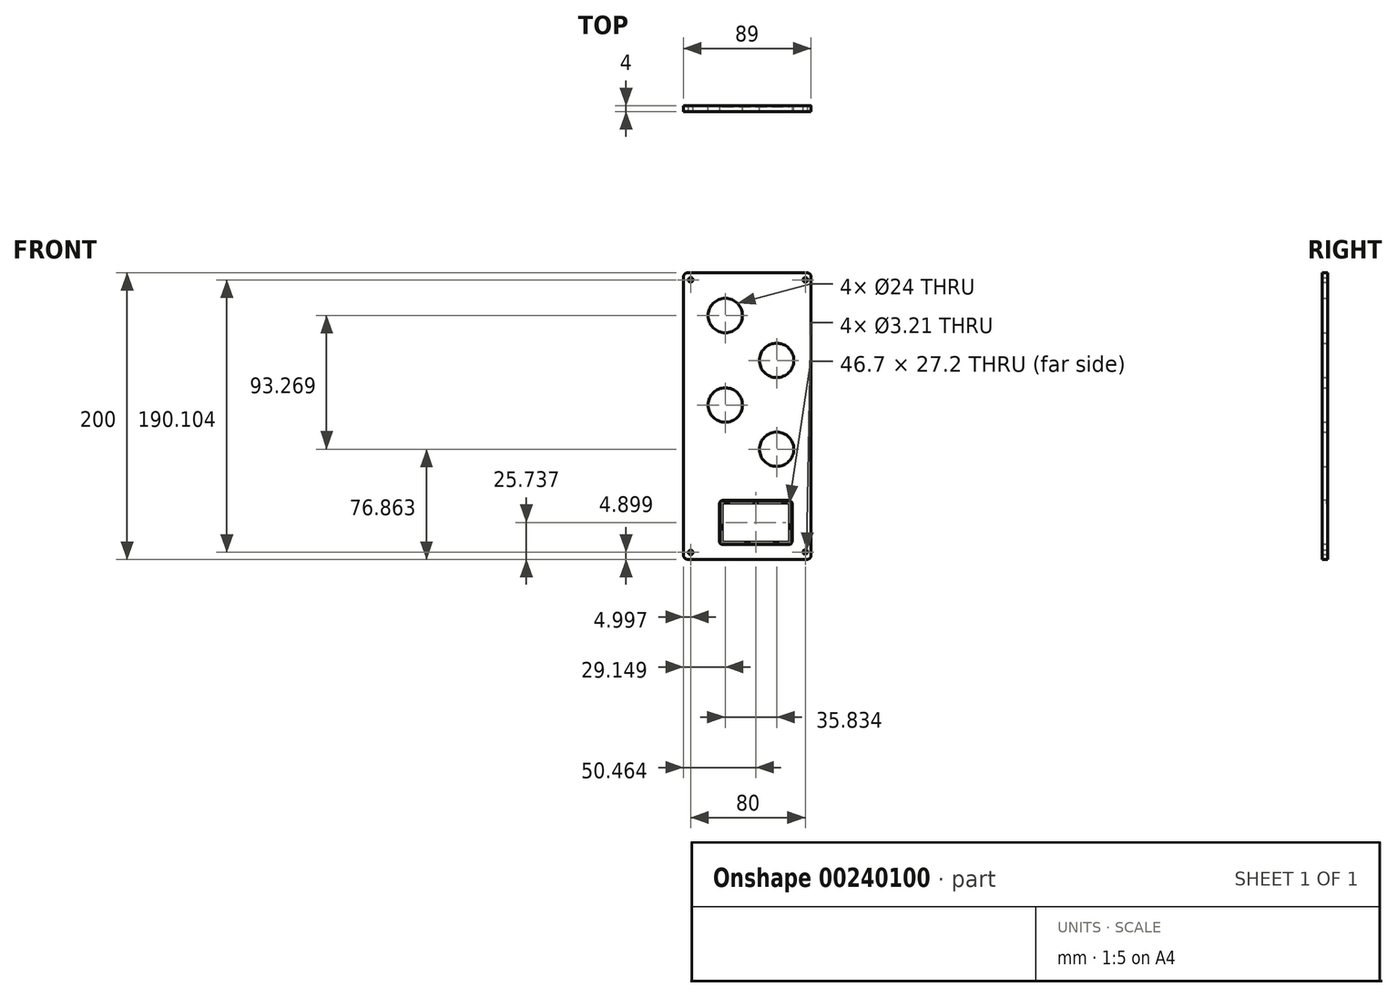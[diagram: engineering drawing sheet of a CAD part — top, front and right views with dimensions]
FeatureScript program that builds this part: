
annotation { "Feature Type Name" : "Feature", "Feature Type Description" : "" }
export const myFeature = defineFeature(function(context is Context, id is Id, definition is map)
    precondition{}
    {
        {
            var Q0;
            Q0=qCreatedBy(makeId("Front.planeOp"),FACE);
            var sketch = newSketch(context, id + "F0", { "sketchPlane" : qUnion([Q0])});
            skLineSegment(sketch, "E0.bottom", {"start": v(-22.42, 158.2) * mm, "end": v(66.58, 158.2) * mm});
            skLineSegment(sketch, "E0.top", {"start": v(-22.42, -41.8) * mm, "end": v(66.58, -41.8) * mm});
            skLineSegment(sketch, "E0.left", {"start": v(-22.42, 158.2) * mm, "end": v(-22.42, -41.8) * mm});
            skLineSegment(sketch, "E0.right", {"start": v(66.58, 158.2) * mm, "end": v(66.58, -41.8) * mm});
            skLineSegment(sketch, "E1.bottom", {"start": v(-17.42, 153.2) * mm, "end": v(62.58, 153.2) * mm, "construction": true});
            skLineSegment(sketch, "E1.top", {"start": v(-17.42, -36.8) * mm, "end": v(62.58, -36.8) * mm, "construction": true});
            skLineSegment(sketch, "E1.left", {"start": v(-17.42, 153.2) * mm, "end": v(-17.42, -36.8) * mm, "construction": true});
            skLineSegment(sketch, "E1.right", {"start": v(62.58, 153.2) * mm, "end": v(62.58, -36.8) * mm, "construction": true});
            skLineSegment(sketch, "E2.bottom", {"start": v(-7.42, 152.2) * mm, "end": v(55.58, 152.2) * mm, "construction": true});
            skLineSegment(sketch, "E2.top", {"start": v(-7.42, -34.8) * mm, "end": v(55.58, -34.8) * mm, "construction": true});
            skLineSegment(sketch, "E2.left", {"start": v(-7.42, 152.2) * mm, "end": v(-7.42, -34.8) * mm, "construction": true});
            skLineSegment(sketch, "E2.right", {"start": v(55.58, 152.2) * mm, "end": v(55.58, -34.8) * mm, "construction": true});
            skCircle(sketch, "E3", {"center": v(6.73, 128.33) * mm, "radius": 23 * mm, "construction": true});
            skCircle(sketch, "E4", {"center": v(6.73, 128.33) * mm, "radius": 12 * mm});
            skCircle(sketch, "E5", {"center": v(42.56, 97.03) * mm, "radius": 23 * mm, "construction": true});
            skCircle(sketch, "E6", {"center": v(42.56, 97.03) * mm, "radius": 12 * mm});
            skCircle(sketch, "E7", {"center": v(6.73, 65.91) * mm, "radius": 23 * mm, "construction": true});
            skCircle(sketch, "E8", {"center": v(6.73, 65.91) * mm, "radius": 12 * mm});
            skCircle(sketch, "E9", {"center": v(42.56, 35.06) * mm, "radius": 23 * mm, "construction": true});
            skCircle(sketch, "E10", {"center": v(42.56, 35.06) * mm, "radius": 12 * mm});
            skLineSegment(sketch, "E11.bottom", {"start": v(4.7, -2.46) * mm, "end": v(51.4, -2.46) * mm});
            skLineSegment(sketch, "E11.top", {"start": v(4.7, -29.66) * mm, "end": v(51.4, -29.66) * mm});
            skLineSegment(sketch, "E11.left", {"start": v(4.7, -2.46) * mm, "end": v(4.7, -29.66) * mm});
            skLineSegment(sketch, "E11.right", {"start": v(51.4, -2.46) * mm, "end": v(51.4, -29.66) * mm});
            skPoint(sketch, "E12", {"position": v(-17.42, 153.2) * mm});
            skPoint(sketch, "E13", {"position": v(62.58, 153.2) * mm});
            skPoint(sketch, "E14", {"position": v(-17.42, -36.8) * mm});
            skPoint(sketch, "E15", {"position": v(62.58, -36.8) * mm});
            skCircle(sketch, "E16", {"center": v(-17.42, 153.2) * mm, "radius": 1.6 * mm});
            skCircle(sketch, "E17", {"center": v(62.58, 153.2) * mm, "radius": 1.6 * mm});
            skCircle(sketch, "E18", {"center": v(62.52, -36.64) * mm, "radius": 1.6 * mm});
            skCircle(sketch, "E19", {"center": v(-17.42, -36.9) * mm, "radius": 1.6 * mm});
            skSolve(sketch);
        }
        {
            var Q0;
            Q0=makeQuery(id+"F0.imprint","IMPRINT",FACE,{"disambiguationData":[TD([[makeQuery(id+"F0.imprint","IMPRINT",EDGE,{"derivedFrom":sQuery(id+"F0.wireOp",EDGE,"E0.bottom")}),-1.0]])]});
            extrude(context, id + "F1", {"entities" : qUnion([Q0]), "depth" : 4 * mm});
        }
        {
            var Q0;
            Q0=makeQuery(id+"F1.opExtrude","SWEPT_EDGE",EDGE,{"disambiguationData":[OSD([sQuery(id+"F0.wireOp",EDGE,"E0.bottom"),sQuery(id+"F0.wireOp",EDGE,"E0.left")])]});
            var Q1;
            Q1=makeQuery(id+"F1.opExtrude","SWEPT_EDGE",EDGE,{"disambiguationData":[OSD([sQuery(id+"F0.wireOp",EDGE,"E0.bottom"),sQuery(id+"F0.wireOp",EDGE,"E0.right")])]});
            var Q2;
            Q2=makeQuery(id+"F1.opExtrude","SWEPT_EDGE",EDGE,{"disambiguationData":[OSD([sQuery(id+"F0.wireOp",EDGE,"E0.top"),sQuery(id+"F0.wireOp",EDGE,"E0.right")])]});
            var Q3;
            Q3=makeQuery(id+"F1.opExtrude","SWEPT_EDGE",EDGE,{"disambiguationData":[OSD([sQuery(id+"F0.wireOp",EDGE,"E0.top"),sQuery(id+"F0.wireOp",EDGE,"E0.left")])]});
            fillet(context, id + "F2", {"entities" : qUnion([Q0, Q1, Q2, Q3]), "radius" : 3 * mm, "tangentPropagation" : true, "allowEdgeOverflow" : false});
        }
        {
            var Q0;
            Q0=makeQuery(id+"F1.opExtrude","CAP_FACE",FACE,{"disambiguationData":[OSD([sQuery(id+"F0.wireOp",EDGE,"E0.bottom"),sQuery(id+"F0.wireOp",EDGE,"E0.top"),sQuery(id+"F0.wireOp",EDGE,"E0.left"),sQuery(id+"F0.wireOp",EDGE,"E0.right"),sQuery(id+"F0.wireOp",EDGE,"E4"),sQuery(id+"F0.wireOp",EDGE,"E6"),sQuery(id+"F0.wireOp",EDGE,"E8"),sQuery(id+"F0.wireOp",EDGE,"E10"),sQuery(id+"F0.wireOp",EDGE,"E11.bottom"),sQuery(id+"F0.wireOp",EDGE,"E11.top"),sQuery(id+"F0.wireOp",EDGE,"E11.left"),sQuery(id+"F0.wireOp",EDGE,"E11.right"),sQuery(id+"F0.wireOp",EDGE,"E16"),sQuery(id+"F0.wireOp",EDGE,"E17"),sQuery(id+"F0.wireOp",EDGE,"E18"),sQuery(id+"F0.wireOp",EDGE,"E19")])],"isStart":false});
            var sketch = newSketch(context, id + "F3", { "sketchPlane" : qUnion([Q0])});
            skLineSegment(sketch, "E20", {"start": v(4.7, -16.06) * mm, "end": v(51.4, -16.06) * mm, "construction": true});
            skLineSegment(sketch, "E21", {"start": v(28.04, -2.46) * mm, "end": v(28.04, -29.66) * mm, "construction": true});
            skLineSegment(sketch, "E22.bottom", {"start": v(2.7, -0.66) * mm, "end": v(53.4, -0.66) * mm});
            skLineSegment(sketch, "E22.top", {"start": v(2.7, -31.46) * mm, "end": v(53.4, -31.46) * mm});
            skLineSegment(sketch, "E22.left", {"start": v(2.7, -0.66) * mm, "end": v(2.7, -31.46) * mm});
            skLineSegment(sketch, "E22.right", {"start": v(53.4, -0.66) * mm, "end": v(53.4, -31.46) * mm});
            skSolve(sketch);
        }
        {
            var Q0;
            Q0 = qSketchRegion(id + "F3", true);
            extrude(context, id + "F4", {"entities" : qUnion([Q0]), "operationType" : NewBodyOperationType.REMOVE, "oppositeDirection" : true, "depth" : 3.25 * mm});
        }
        {
            var Q0;
            Q0=makeQuery(id+"F4.boolean.opBoolean","COPY",EDGE,{"derivedFrom":makeQuery(id+"F4.opExtrude","SWEPT_EDGE",EDGE,{"disambiguationData":[OSD([sQuery(id+"F3.wireOp",EDGE,"E22.bottom"),sQuery(id+"F3.wireOp",EDGE,"E22.left")])]})});
            var Q1;
            Q1=makeQuery(id+"F4.boolean.opBoolean","COPY",EDGE,{"derivedFrom":makeQuery(id+"F4.opExtrude","SWEPT_EDGE",EDGE,{"disambiguationData":[OSD([sQuery(id+"F3.wireOp",EDGE,"E22.top"),sQuery(id+"F3.wireOp",EDGE,"E22.right")])]})});
            var Q2;
            Q2=makeQuery(id+"F4.boolean.opBoolean","COPY",EDGE,{"derivedFrom":makeQuery(id+"F4.opExtrude","SWEPT_EDGE",EDGE,{"disambiguationData":[OSD([sQuery(id+"F3.wireOp",EDGE,"E22.top"),sQuery(id+"F3.wireOp",EDGE,"E22.left")])]})});
            var Q3;
            Q3=makeQuery(id+"F4.boolean.opBoolean","COPY",EDGE,{"derivedFrom":makeQuery(id+"F4.opExtrude","SWEPT_EDGE",EDGE,{"disambiguationData":[OSD([sQuery(id+"F3.wireOp",EDGE,"E22.bottom"),sQuery(id+"F3.wireOp",EDGE,"E22.right")])]})});
            fillet(context, id + "F5", {"entities" : qUnion([Q0, Q1, Q2, Q3]), "radius" : 2.4 * mm, "tangentPropagation" : true, "allowEdgeOverflow" : false});
        }
    });
